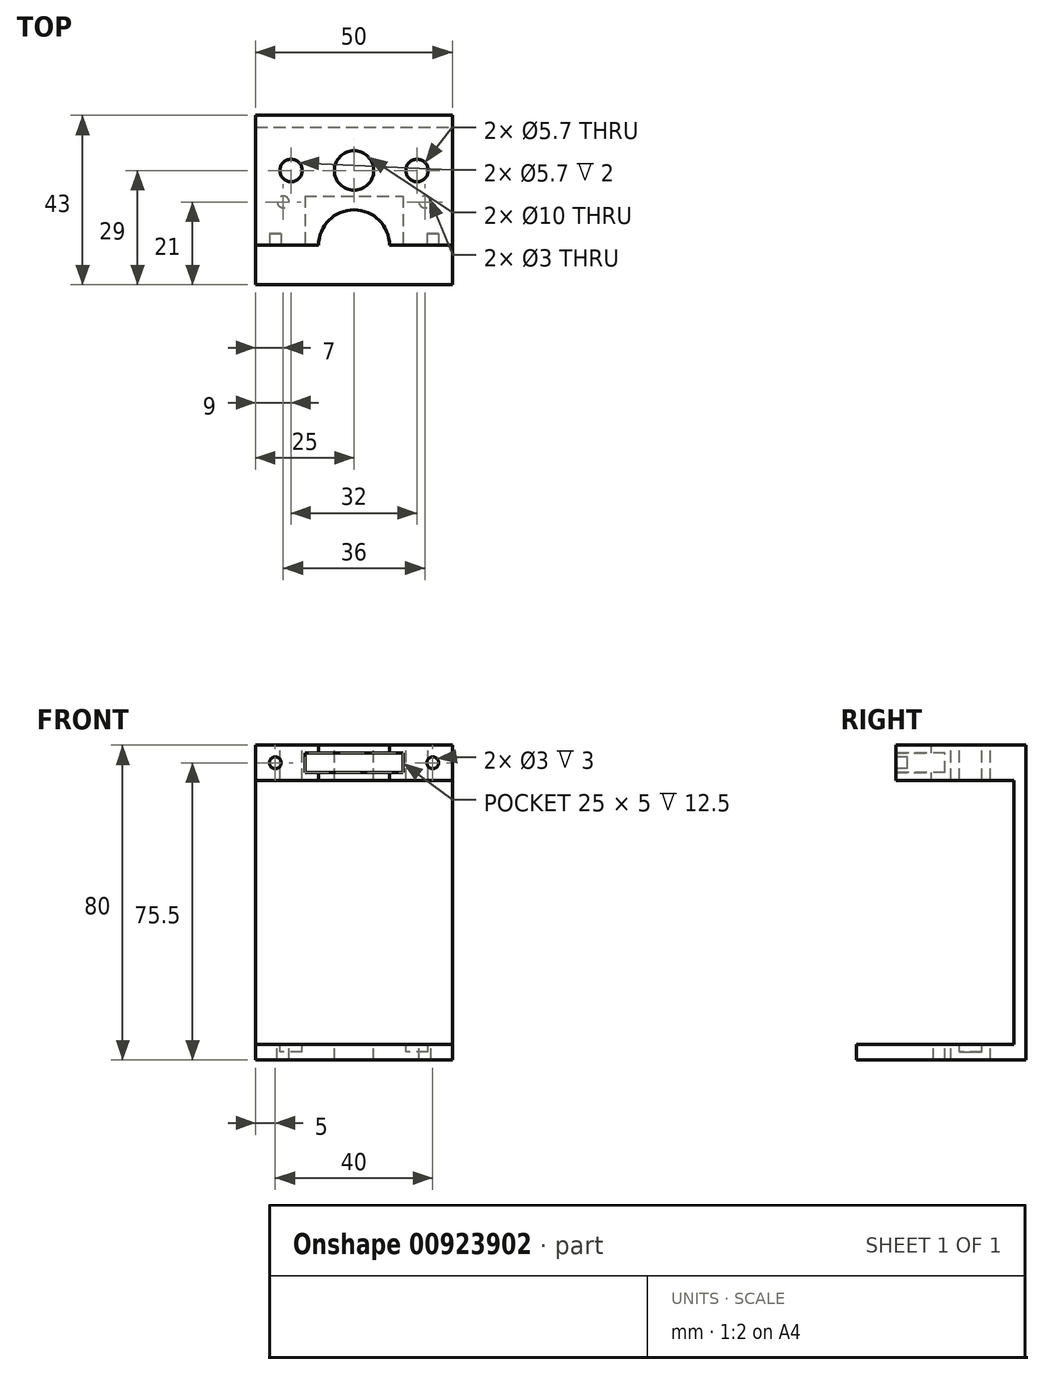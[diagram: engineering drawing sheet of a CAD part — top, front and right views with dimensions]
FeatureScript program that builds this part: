
annotation { "Feature Type Name" : "Feature", "Feature Type Description" : "" }
export const myFeature = defineFeature(function(context is Context, id is Id, definition is map)
    precondition{}
    {
        {
            var Q0;
            Q0=qCreatedBy(makeId("Front.planeOp"),FACE);
            var sketch = newSketch(context, id + "F0", { "sketchPlane" : qUnion([Q0])});
            skLineSegment(sketch, "E0.bottom", {"start": v(0, 0) * mm, "end": v(50, 0) * mm});
            skLineSegment(sketch, "E0.top", {"start": v(0, 80) * mm, "end": v(50, 80) * mm});
            skLineSegment(sketch, "E0.left", {"start": v(0, 0) * mm, "end": v(0, 80) * mm});
            skLineSegment(sketch, "E0.right", {"start": v(50, 0) * mm, "end": v(50, 80) * mm});
            skSolve(sketch);
        }
        {
            var Q0;
            Q0 = qSketchRegion(id + "F0", true);
            extrude(context, id + "F1", {"entities" : qUnion([Q0]), "depth" : 3 * mm, "offsetDistance" : 25 * mm});
        }
        {
            var Q0;
            Q0=makeQuery(id+"F1.opExtrude","CAP_FACE",FACE,{"disambiguationData":[OSD([sQuery(id+"F0.wireOp",EDGE,"E0.bottom"),sQuery(id+"F0.wireOp",EDGE,"E0.top"),sQuery(id+"F0.wireOp",EDGE,"E0.left"),sQuery(id+"F0.wireOp",EDGE,"E0.right")])],"isStart":false});
            var sketch = newSketch(context, id + "F2", { "sketchPlane" : qUnion([Q0])});
            skLineSegment(sketch, "E1", {"start": v(0, 4) * mm, "end": v(50, 4) * mm});
            skLineSegment(sketch, "E2", {"start": v(0, 71) * mm, "end": v(50, 71) * mm});
            skSolve(sketch);
        }
        {
            var Q0;
            {var subQ0=sQuery(id+"F2.wireOp",EDGE,"E1");Q0=makeQuery(id+"F2.imprint","IMPRINT",FACE,{"disambiguationData":[TD([[makeQuery(id+"F2.imprint","IMPRINT",EDGE,{"derivedFrom":subQ0}),-1.0]])]});}
            extrude(context, id + "F3", {"entities" : qUnion([Q0]), "operationType" : NewBodyOperationType.ADD, "depth" : 40 * mm, "offsetDistance" : 25 * mm});
        }
        {
            var Q0;
            {var subQ0=sQuery(id+"F2.wireOp",EDGE,"E2");Q0=makeQuery(id+"F2.imprint","IMPRINT",FACE,{"disambiguationData":[TD([[makeQuery(id+"F2.imprint","IMPRINT",EDGE,{"derivedFrom":subQ0}),1.0]])]});}
            extrude(context, id + "F4", {"entities" : qUnion([Q0]), "operationType" : NewBodyOperationType.ADD, "depth" : 30 * mm, "offsetDistance" : 25 * mm});
        }
        {
            var Q0;
            Q0=makeQuery(id+"F4.opExtrude","CAP_FACE",FACE,{"disambiguationData":[OSD([sQuery(id+"F0.wireOp",EDGE,"E0.top"),sQuery(id+"F0.wireOp",EDGE,"E0.left"),sQuery(id+"F0.wireOp",EDGE,"E0.right"),sQuery(id+"F2.wireOp",EDGE,"E2")])],"isStart":false});
            var sketch = newSketch(context, id + "F5", { "sketchPlane" : qUnion([Q0])});
            skLineSegment(sketch, "E3.bottom", {"start": v(12.5, 73) * mm, "end": v(37.5, 73) * mm});
            skLineSegment(sketch, "E3.top", {"start": v(12.5, 78) * mm, "end": v(37.5, 78) * mm});
            skLineSegment(sketch, "E3.left", {"start": v(12.5, 73) * mm, "end": v(12.5, 78) * mm});
            skLineSegment(sketch, "E3.right", {"start": v(37.5, 73) * mm, "end": v(37.5, 78) * mm});
            skSolve(sketch);
        }
        {
            var Q0;
            Q0=makeQuery(id+"F5.imprint","IMPRINT",FACE,{"disambiguationData":[TD([[makeQuery(id+"F5.imprint","IMPRINT",EDGE,{"derivedFrom":sQuery(id+"F5.wireOp",EDGE,"E3.bottom")}),1.0]])]});
            extrude(context, id + "F6", {"entities" : qUnion([Q0]), "operationType" : NewBodyOperationType.REMOVE, "oppositeDirection" : true, "depth" : 12.5 * mm, "offsetDistance" : 25 * mm});
        }
        {
            var Q0;
            {var subQ0=sQuery(id+"F0.wireOp",EDGE,"E0.top");Q0=makeQuery(id+"F4.boolean.opBoolean","MERGE",FACE,{"derivedFrom":[makeQuery(id+"F1.opExtrude","SWEPT_FACE",FACE,{"disambiguationData":[OSD([subQ0])]}),makeQuery(id+"F4.opExtrude","SWEPT_FACE",FACE,{"disambiguationData":[OSD([subQ0])]})]});}
            var sketch = newSketch(context, id + "F7", { "sketchPlane" : qUnion([Q0])});
            skCircle(sketch, "E4", {"center": v(25, -33) * mm, "radius": 9 * mm});
            skCircle(sketch, "E5", {"center": v(9, -14) * mm, "radius": 2.85 * mm});
            skCircle(sketch, "E6", {"center": v(41, -14) * mm, "radius": 2.85 * mm});
            skCircle(sketch, "E7", {"center": v(25, -14) * mm, "radius": 5 * mm});
            skSolve(sketch);
        }
        {
            var Q0;
            {var subQ0=sQuery(id+"F7.wireOp",EDGE,"E4");var subQ1=makeQuery(id+"F4.opExtrude","CAP_EDGE",EDGE,{"disambiguationData":[OSD([sQuery(id+"F0.wireOp",EDGE,"E0.top")])],"isStart":false});var subQ2=makeQuery(id+"F7.imprint","INTERSECT",VERTEX,{"disambiguationData":[OD(0.0)],"derivedFrom":[subQ1,subQ0]});Q0=makeQuery(id+"F7.imprint","IMPRINT",FACE,{"disambiguationData":[TD([[makeQuery(id+"F7.imprint","IMPRINT",EDGE,{"disambiguationData":[TD([[subQ2,1.0]])],"derivedFrom":subQ0}),1.0]])]});}
            extrude(context, id + "F8", {"entities" : qUnion([Q0]), "operationType" : NewBodyOperationType.REMOVE, "oppositeDirection" : true, "depth" : 9 * mm, "offsetDistance" : 25 * mm});
        }
        {
            var Q0;
            {var subQ0=sQuery(id+"F2.wireOp",EDGE,"E2");var subQ1=sQuery(id+"F0.wireOp",EDGE,"E0.right");var subQ2=sQuery(id+"F0.wireOp",EDGE,"E0.top");Q0=makeQuery(id+"F8.boolean.opBoolean","SPLIT",FACE,{"disambiguationData":[TD([makeQuery(id+"F1.opExtrude","SWEPT_FACE",FACE,{"disambiguationData":[OSD([subQ1])]})])],"derivedFrom":makeQuery(id+"F4.opExtrude","CAP_FACE",FACE,{"disambiguationData":[OSD([subQ2,sQuery(id+"F0.wireOp",EDGE,"E0.left"),subQ1,subQ0])],"isStart":false})});}
            var sketch = newSketch(context, id + "F9", { "sketchPlane" : qUnion([Q0])});
            skCircle(sketch, "E8", {"center": v(5, 75.5) * mm, "radius": 1.5 * mm});
            skCircle(sketch, "E9", {"center": v(45, 75.5) * mm, "radius": 1.5 * mm});
            skSolve(sketch);
        }
        {
            var Q0;
            Q0=makeQuery(id+"F9.imprint","IMPRINT",FACE,{"disambiguationData":[TD([[makeQuery(id+"F9.imprint","IMPRINT",EDGE,{"derivedFrom":sQuery(id+"F9.wireOp",EDGE,"E8")}),1.0]])]});
            var Q1;
            Q1=makeQuery(id+"F9.imprint","IMPRINT",FACE,{"disambiguationData":[TD([[makeQuery(id+"F9.imprint","IMPRINT",EDGE,{"derivedFrom":sQuery(id+"F9.wireOp",EDGE,"E9")}),1.0]])]});
            extrude(context, id + "F10", {"entities" : qUnion([Q0, Q1]), "operationType" : NewBodyOperationType.REMOVE, "oppositeDirection" : true, "depth" : 3 * mm, "offsetDistance" : 25 * mm});
        }
        {
            var Q0;
            Q0=makeQuery(id+"F7.imprint","IMPRINT",FACE,{"disambiguationData":[TD([[makeQuery(id+"F7.imprint","IMPRINT",EDGE,{"derivedFrom":sQuery(id+"F7.wireOp",EDGE,"E5")}),1.0]])]});
            var Q1;
            Q1=makeQuery(id+"F7.imprint","IMPRINT",FACE,{"disambiguationData":[TD([[makeQuery(id+"F7.imprint","IMPRINT",EDGE,{"derivedFrom":sQuery(id+"F7.wireOp",EDGE,"E6")}),1.0]])]});
            extrude(context, id + "F11", {"entities" : qUnion([Q0, Q1]), "operationType" : NewBodyOperationType.REMOVE, "oppositeDirection" : true, "depth" : 78 * mm, "offsetDistance" : 25 * mm});
        }
        {
            var Q0;
            Q0=makeQuery(id+"F7.imprint","IMPRINT",FACE,{"disambiguationData":[TD([[makeQuery(id+"F7.imprint","IMPRINT",EDGE,{"derivedFrom":sQuery(id+"F7.wireOp",EDGE,"E7")}),1.0]])]});
            extrude(context, id + "F12", {"entities" : qUnion([Q0]), "operationType" : NewBodyOperationType.REMOVE, "oppositeDirection" : true, "depth" : 80 * mm, "offsetDistance" : 25 * mm});
        }
        {
            var Q0;
            Q0=makeQuery(id+"F3.opExtrude","SWEPT_FACE",FACE,{"disambiguationData":[OSD([sQuery(id+"F2.wireOp",EDGE,"E1")])]});
            var sketch = newSketch(context, id + "F13", { "sketchPlane" : qUnion([Q0])});
            skCircle(sketch, "E10", {"center": v(43, -22) * mm, "radius": 1.5 * mm});
            skCircle(sketch, "E11", {"center": v(7, -22) * mm, "radius": 1.5 * mm});
            skSolve(sketch);
        }
        {
            var Q0;
            Q0=makeQuery(id+"F13.imprint","IMPRINT",FACE,{"disambiguationData":[TD([[makeQuery(id+"F13.imprint","IMPRINT",EDGE,{"derivedFrom":sQuery(id+"F13.wireOp",EDGE,"E11")}),1.0]])]});
            var Q1;
            Q1=makeQuery(id+"F13.imprint","IMPRINT",FACE,{"disambiguationData":[TD([[makeQuery(id+"F13.imprint","IMPRINT",EDGE,{"derivedFrom":sQuery(id+"F13.wireOp",EDGE,"E10")}),1.0]])]});
            extrude(context, id + "F14", {"entities" : qUnion([Q0, Q1]), "operationType" : NewBodyOperationType.REMOVE, "oppositeDirection" : true, "depth" : 4 * mm, "offsetDistance" : 25 * mm});
        }
    });
